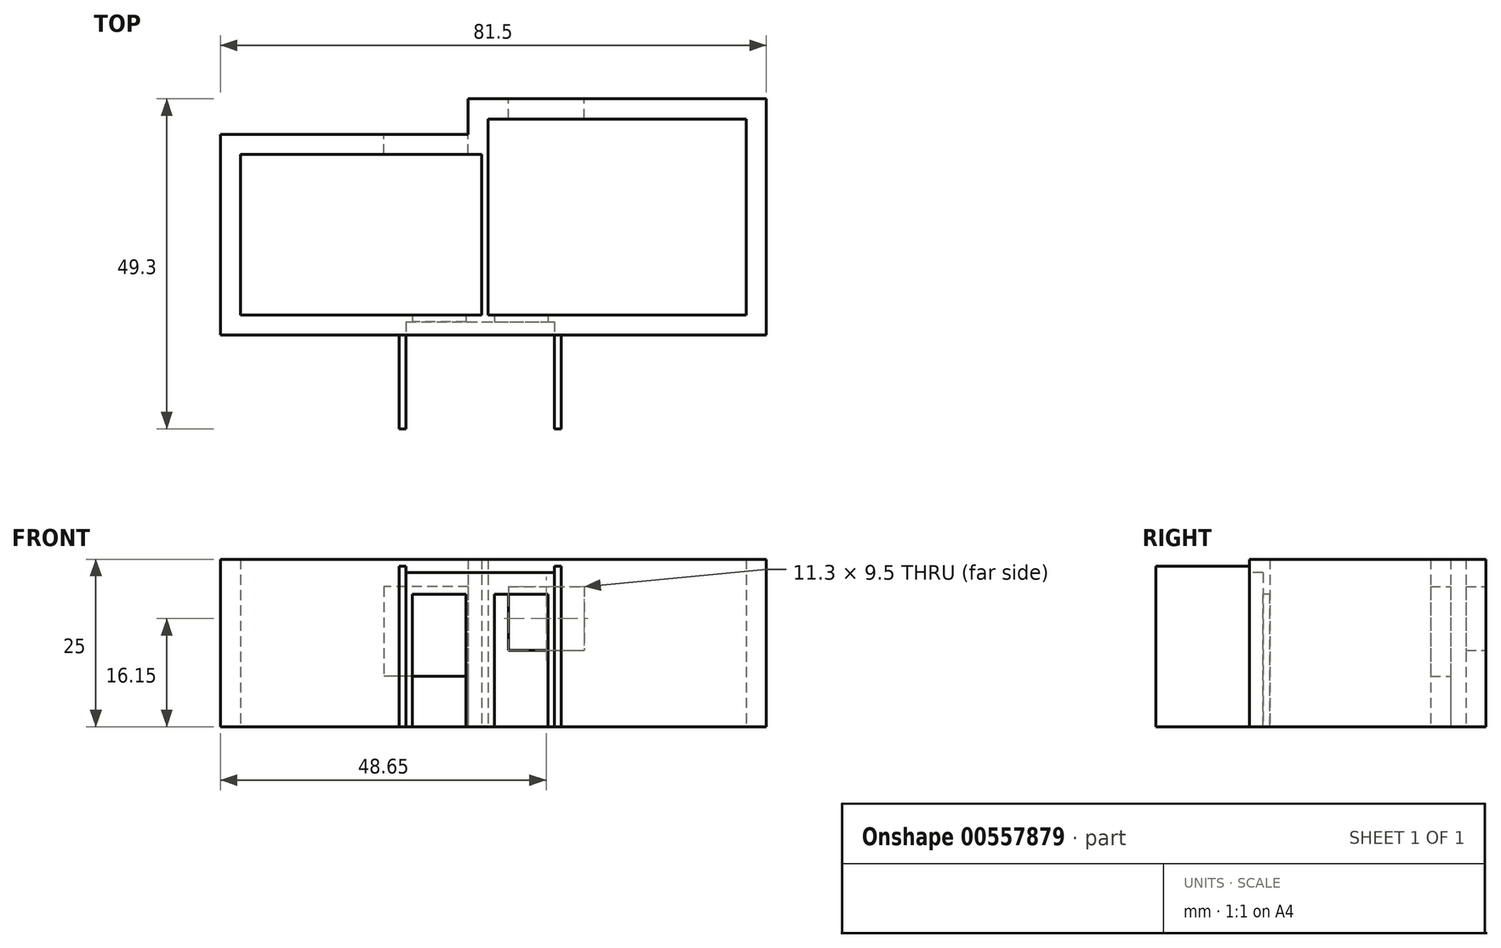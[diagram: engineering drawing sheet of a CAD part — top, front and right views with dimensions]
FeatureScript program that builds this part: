
annotation { "Feature Type Name" : "Feature", "Feature Type Description" : "" }
export const myFeature = defineFeature(function(context is Context, id is Id, definition is map)
    precondition{}
    {
        {
            var Q0;
            Q0=qCreatedBy(makeId("Top.planeOp"),FACE);
            var sketch = newSketch(context, id + "F0", { "sketchPlane" : qUnion([Q0])});
            skLineSegment(sketch, "E0", {"start": v(0, 0) * mm, "end": v(36, 0) * mm});
            skLineSegment(sketch, "E1", {"start": v(75.5, 0) * mm, "end": v(75.5, 29.3) * mm});
            skLineSegment(sketch, "E2", {"start": v(75.5, 29.3) * mm, "end": v(37, 29.3) * mm});
            skLineSegment(sketch, "E3", {"start": v(37, 29.3) * mm, "end": v(37, 24) * mm});
            skLineSegment(sketch, "E4", {"start": v(36, 24) * mm, "end": v(0, 24) * mm});
            skLineSegment(sketch, "E5", {"start": v(0, 24) * mm, "end": v(0, 0) * mm});
            skLineSegment(sketch, "E6.0", {"start": v(34, 27) * mm, "end": v(-3, 27) * mm});
            skLineSegment(sketch, "E6.1", {"start": v(-3, -3) * mm, "end": v(78.5, -3) * mm});
            skLineSegment(sketch, "E6.2", {"start": v(78.5, -3) * mm, "end": v(78.5, 32.3) * mm});
            skLineSegment(sketch, "E6.3", {"start": v(-3, 27) * mm, "end": v(-3, -3) * mm});
            skLineSegment(sketch, "E6.4", {"start": v(78.5, 32.3) * mm, "end": v(34, 32.3) * mm});
            skLineSegment(sketch, "E6.5", {"start": v(34, 32.3) * mm, "end": v(34, 27) * mm});
            skLineSegment(sketch, "E7", {"start": v(37, 24) * mm, "end": v(37, 0) * mm});
            skLineSegment(sketch, "E8.0", {"start": v(36, 24) * mm, "end": v(36, 0) * mm});
            skLineSegment(sketch, "E9.trimOffspring", {"start": v(37, 0) * mm, "end": v(75.5, 0) * mm});
            skSolve(sketch);
        }
        {
            var Q0;
            Q0 = qSketchRegion(id + "F0", true);
            extrude(context, id + "F1", {"entities" : qUnion([Q0]), "depth" : 25 * mm, "offsetDistance" : 25 * mm});
        }
        {
            var Q0;
            Q0=makeQuery(id+"F1.opExtrude","CAP_FACE",FACE,{"disambiguationData":[OSD([sQuery(id+"F0.wireOp",EDGE,"E0"),sQuery(id+"F0.wireOp",EDGE,"E1"),sQuery(id+"F0.wireOp",EDGE,"E2"),sQuery(id+"F0.wireOp",EDGE,"E3"),sQuery(id+"F0.wireOp",EDGE,"E4"),sQuery(id+"F0.wireOp",EDGE,"E5"),sQuery(id+"F0.wireOp",EDGE,"E6.0"),sQuery(id+"F0.wireOp",EDGE,"E6.1"),sQuery(id+"F0.wireOp",EDGE,"E6.2"),sQuery(id+"F0.wireOp",EDGE,"E6.3"),sQuery(id+"F0.wireOp",EDGE,"E6.4"),sQuery(id+"F0.wireOp",EDGE,"E6.5"),sQuery(id+"F0.wireOp",EDGE,"E7"),sQuery(id+"F0.wireOp",EDGE,"E8.0"),sQuery(id+"F0.wireOp",EDGE,"E9.trimOffspring")])],"isStart":true});
            var sketch = newSketch(context, id + "F2", { "sketchPlane" : qUnion([Q0])});
            skLineSegment(sketch, "E10.bottom", {"start": v(24.7, 0) * mm, "end": v(23.7, 0) * mm});
            skLineSegment(sketch, "E10.top", {"start": v(24.7, 17) * mm, "end": v(23.7, 17) * mm});
            skLineSegment(sketch, "E10.left", {"start": v(24.7, 0) * mm, "end": v(24.7, 17) * mm});
            skLineSegment(sketch, "E10.right", {"start": v(23.7, 0) * mm, "end": v(23.7, 17) * mm});
            skLineSegment(sketch, "E11.bottom", {"start": v(46.9, 0) * mm, "end": v(47.9, 0) * mm});
            skLineSegment(sketch, "E11.top", {"start": v(46.9, 17) * mm, "end": v(47.9, 17) * mm});
            skLineSegment(sketch, "E11.left", {"start": v(46.9, 0) * mm, "end": v(46.9, 17) * mm});
            skLineSegment(sketch, "E11.right", {"start": v(47.9, 0) * mm, "end": v(47.9, 17) * mm});
            skSolve(sketch);
        }
        {
            var Q0;
            Q0 = qSketchRegion(id + "F2", true);
            extrude(context, id + "F3", {"entities" : qUnion([Q0]), "operationType" : NewBodyOperationType.ADD, "oppositeDirection" : true, "depth" : 24 * mm, "offsetDistance" : 25 * mm});
        }
        {
            var Q0;
            Q0=makeQuery(id+"F1.opExtrude","SWEPT_FACE",FACE,{"disambiguationData":[OSD([sQuery(id+"F0.wireOp",EDGE,"E6.1")])]});
            var sketch = newSketch(context, id + "F4", { "sketchPlane" : qUnion([Q0])});
            skLineSegment(sketch, "E12.bottom", {"start": v(24.7, 0) * mm, "end": v(46.9, 0) * mm});
            skLineSegment(sketch, "E12.top", {"start": v(24.7, 23) * mm, "end": v(46.9, 23) * mm});
            skLineSegment(sketch, "E12.left", {"start": v(24.7, 0) * mm, "end": v(24.7, 23) * mm});
            skLineSegment(sketch, "E12.right", {"start": v(46.9, 0) * mm, "end": v(46.9, 23) * mm});
            skSolve(sketch);
        }
        {
            var Q0;
            Q0 = qSketchRegion(id + "F4", true);
            extrude(context, id + "F5", {"entities" : qUnion([Q0]), "operationType" : NewBodyOperationType.REMOVE, "oppositeDirection" : true, "depth" : 2 * mm, "offsetDistance" : 25 * mm});
        }
        {
            var Q0;
            Q0=makeQuery(id+"F5.boolean.opBoolean","COPY",FACE,{"derivedFrom":makeQuery(id+"F5.opExtrude","CAP_FACE",FACE,{"disambiguationData":[OSD([sQuery(id+"F4.wireOp",EDGE,"E12.bottom"),sQuery(id+"F4.wireOp",EDGE,"E12.top"),sQuery(id+"F4.wireOp",EDGE,"E12.left"),sQuery(id+"F4.wireOp",EDGE,"E12.right")])],"isStart":false})});
            var sketch = newSketch(context, id + "F6", { "sketchPlane" : qUnion([Q0])});
            skLineSegment(sketch, "E13.bottom", {"start": v(37.9, 0) * mm, "end": v(45.9, 0) * mm});
            skLineSegment(sketch, "E13.top", {"start": v(37.9, 19.8) * mm, "end": v(45.9, 19.8) * mm});
            skLineSegment(sketch, "E13.left", {"start": v(37.9, 0) * mm, "end": v(37.9, 19.8) * mm});
            skLineSegment(sketch, "E13.right", {"start": v(45.9, 0) * mm, "end": v(45.9, 19.8) * mm});
            skLineSegment(sketch, "E14.bottom", {"start": v(33.7, 0) * mm, "end": v(25.7, 0) * mm});
            skLineSegment(sketch, "E14.top", {"start": v(33.7, 19.8) * mm, "end": v(25.7, 19.8) * mm});
            skLineSegment(sketch, "E14.left", {"start": v(33.7, 0) * mm, "end": v(33.7, 19.8) * mm});
            skLineSegment(sketch, "E14.right", {"start": v(25.7, 0) * mm, "end": v(25.7, 19.8) * mm});
            skSolve(sketch);
        }
        {
            var Q0;
            Q0 = qSketchRegion(id + "F6", true);
            extrude(context, id + "F7", {"entities" : qUnion([Q0]), "operationType" : NewBodyOperationType.REMOVE, "endBound" : BoundingType.UP_TO_NEXT, "oppositeDirection" : true, "depth" : 25 * mm, "offsetDistance" : 25 * mm});
        }
        {
            var Q0;
            Q0=makeQuery(id+"F1.opExtrude","SWEPT_FACE",FACE,{"disambiguationData":[OSD([sQuery(id+"F0.wireOp",EDGE,"E6.0")])]});
            var sketch = newSketch(context, id + "F8", { "sketchPlane" : qUnion([Q0])});
            skLineSegment(sketch, "E15.bottom", {"start": v(-34, 20.9) * mm, "end": v(-21.4, 20.9) * mm});
            skLineSegment(sketch, "E15.top", {"start": v(-34, 7.5) * mm, "end": v(-21.4, 7.5) * mm});
            skLineSegment(sketch, "E15.left", {"start": v(-34, 20.9) * mm, "end": v(-34, 7.5) * mm});
            skLineSegment(sketch, "E15.right", {"start": v(-21.4, 20.9) * mm, "end": v(-21.4, 7.5) * mm});
            skSolve(sketch);
        }
        {
            var Q0;
            Q0 = qSketchRegion(id + "F8", true);
            extrude(context, id + "F9", {"entities" : qUnion([Q0]), "operationType" : NewBodyOperationType.REMOVE, "endBound" : BoundingType.UP_TO_NEXT, "oppositeDirection" : true, "depth" : 25 * mm, "offsetDistance" : 25 * mm});
        }
        {
            var Q0;
            Q0=makeQuery(id+"F1.opExtrude","SWEPT_FACE",FACE,{"disambiguationData":[OSD([sQuery(id+"F0.wireOp",EDGE,"E6.4")])]});
            var sketch = newSketch(context, id + "F10", { "sketchPlane" : qUnion([Q0])});
            skLineSegment(sketch, "E16.bottom", {"start": v(-40, 20.9) * mm, "end": v(-51.3, 20.9) * mm});
            skLineSegment(sketch, "E16.top", {"start": v(-40, 11.4) * mm, "end": v(-51.3, 11.4) * mm});
            skLineSegment(sketch, "E16.left", {"start": v(-40, 20.9) * mm, "end": v(-40, 11.4) * mm});
            skLineSegment(sketch, "E16.right", {"start": v(-51.3, 20.9) * mm, "end": v(-51.3, 11.4) * mm});
            skSolve(sketch);
        }
        {
            var Q0;
            Q0 = qSketchRegion(id + "F10", true);
            extrude(context, id + "F11", {"entities" : qUnion([Q0]), "operationType" : NewBodyOperationType.REMOVE, "endBound" : BoundingType.UP_TO_NEXT, "oppositeDirection" : true, "depth" : 25 * mm, "offsetDistance" : 25 * mm});
        }
    });
